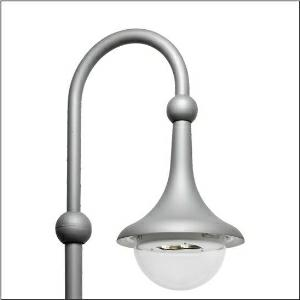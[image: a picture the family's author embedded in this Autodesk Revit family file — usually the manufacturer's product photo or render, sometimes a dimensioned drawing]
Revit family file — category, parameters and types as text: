
# Revit family: grosse_glocke___st1_2a_5xa1563k1b108_1a11
name_source: partatom
category: Lighting Fixtures
units: mm (PartAtom-declared; Revit-internal decimal feet)

## family parameters
Cut with Voids When Loaded = No
Host = Face
Light Source = No
Part Type = Normal
Room Calculation Point = No
Round Connector Dimension = Use Diameter
Shared = No

## types (1)
- --- (1 x LED, 3320 lm, 23.4 W, 4000K)
    Apparent Load = 23 VA
    CIE Flux Codes = 29 66 95 99 100
    Color Rendering = 70
    Color Temperature = 4000K
    Default Elevation = 1800 mm
    Description = Large Bell, mast luminaire, primary light control with 3 zone facetted reflector, of plastic, silver coated, primary optical cover: enclosure, of PMMA, transparent, light distribution: ST1.2a, light emission: direct distribution, primary light characteristic: asymmetric, installation type: suspended mounting, LED, High Power LED, rated luminous flux: 3.320lm, luminous efficacy: 142lm/W, light colour: 740, colour temperature: 4000K, control gear: Plus, control: flexible luminous flux parameterisation, time-dependent luminous flux control, constant luminous flux control, digital communication interface, power reduction, electronic power reduction, mains connection: 230..240V, AC, 50/60Hz, start of lifetime: 23W, end of service life: 24W, reduction: 12W, luminaire housing, bell-shaped, of glass-fibre reinforced polyester, coated, Siteco® metallic grey (DB 702S), please order curved mast extension separately, diameter: 530mm, height: 695mm, mounting height: 4..6m, protection rating (complete): IP54, insulation class (complete): insulation class II (safety insulation), certification: CE, ENEC, VDE, impact resistance: IK08, standard-compliant lighting for roads and squares, packaging unit: 1 piece

Light Distribution: ST1.2a
    Height = 695 mm
    Lamp = 1 x LED
    Lamp Light Flux = 3320 lm
    Lamp Power = 23.4 W
    Lamp count = 1
    Length = 530 mm
    Luminous efficacy = 142 lm/W
    Manufacturer = Siteco
    ModVariant = No
    Model = 5XA1563K1B108
    Number of Poles = 1
    OnlyDefault = Yes
    Power Factor = 1
    Product Name = Große Glocke | ST1.2a
    Product group = mast luminaire | pylon annexe
    ProductGroupID = 6201
    Protection Class = Protection class II
    Protection Degree = IP 54
    RLX_Detail_Level = 1
    RLX_Emergency_Light_Flux = 0 lm
    RLX_Emergency_Type = 0
    RLX_Emergency_Type_DB = No
    RlxData = <blob elided: 52781 chars, md5=e4afe5d2>
    Socket = socket
    Standby Power = 0 W
    System Light Flux = 3320 lm
    System Power = 23 W
    Type Comments = factory setting: luminous flux: 100 % | dim-lin: 254 | 460 mA
    Type Image = l_1347688.jpg
    URL = http://relux.com
    VarID = @adj_197828
    Voltage = 0 V
    Weight = 0.00 kg
    Width = 0 mm  [stored 0 ft]

note: [stored X ft] marks values corroborated as IEEE doubles in the binary element streams (Revit-internal decimal feet)

## geometry (parser evidence)
native form markers: Blend x4, Sweep x10
no freeform markers — native parametric forms only
